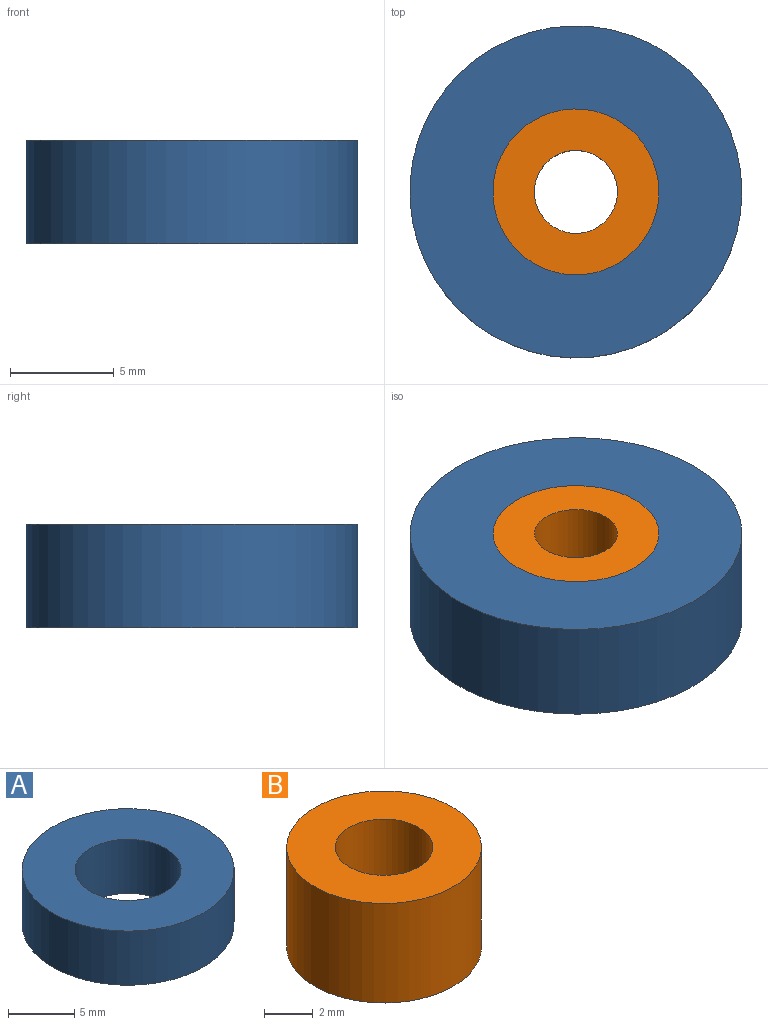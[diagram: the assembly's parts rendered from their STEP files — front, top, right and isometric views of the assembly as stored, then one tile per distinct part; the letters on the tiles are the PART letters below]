
ASSEMBLY  parts=2 mates=1
PART A: 4 faces, bbox 16x16x5 mm
  f0: cylinder r=4mm len=8mm, axis (0,0,-1), area 125.7mm2, adj f2,f3
  f1: cylinder r=8mm len=16mm, axis (0,0,-1), area 251.3mm2, adj f2,f3
  f2: plane 16x16mm, normal (0,0,1), area 150.8mm2, adj f0,f1
  f3: plane 16x16mm, normal (0,0,-1), area 150.8mm2, adj f0,f1
PART B: 4 faces, bbox 8x8x5 mm
  f0: cylinder r=2mm len=5mm, axis (0,0,-1), area 62.8mm2, adj f2,f3
  f1: cylinder r=4mm len=8mm, axis (0,0,-1), area 125.7mm2, adj f2,f3
  f2: plane 8x8mm, normal (0,0,1), area 37.7mm2, adj f0,f1
  f3: plane 8x8mm, normal (0,0,-1), area 37.7mm2, adj f0,f1
PLACE A t=(-7.87,-0.95,5.39)mm
PLACE B t=(-7.87,-0.95,5.39)mm
MATE revolute B.f0 <-> A.f0  axis (0,0,1) through (-7.87,-0.95,10.39)mm
